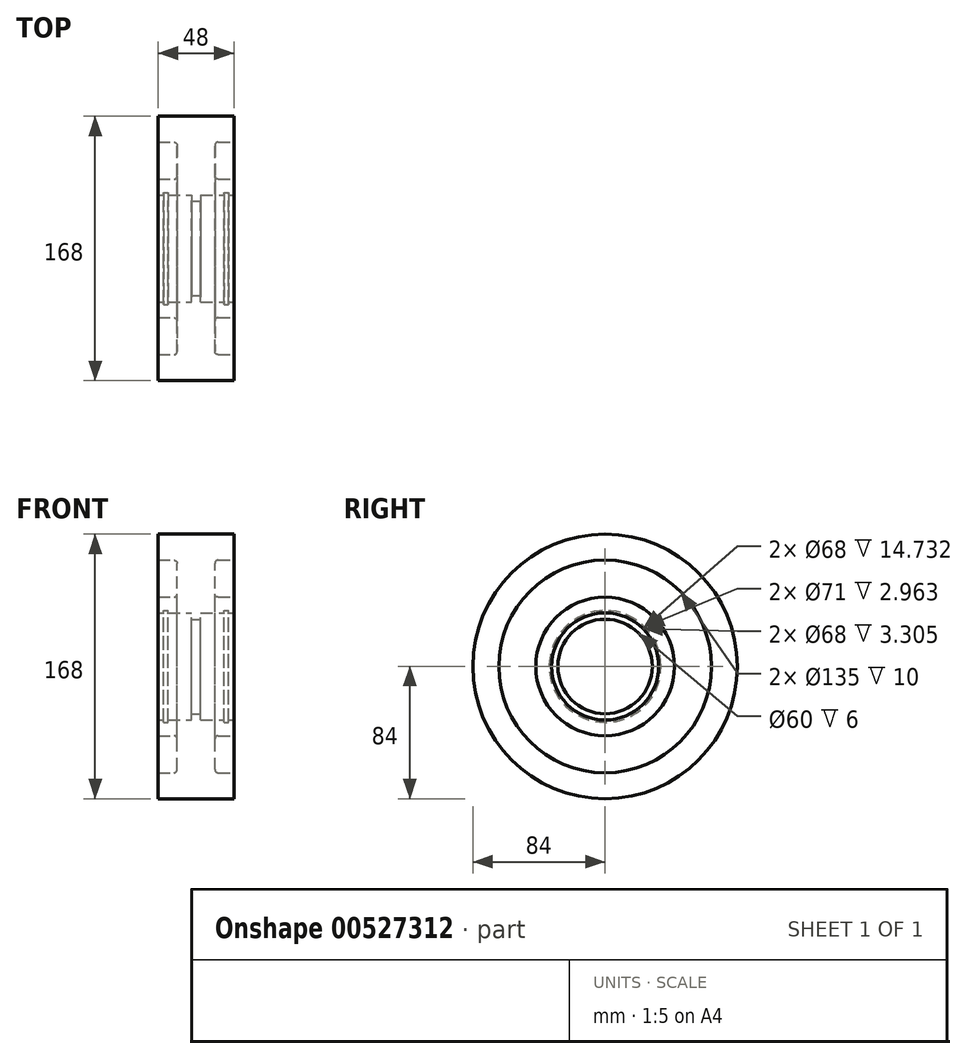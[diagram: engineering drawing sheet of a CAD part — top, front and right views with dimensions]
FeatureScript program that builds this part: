
annotation { "Feature Type Name" : "Feature", "Feature Type Description" : "" }
export const myFeature = defineFeature(function(context is Context, id is Id, definition is map)
    precondition{}
    {
        {
            var Q0;
            Q0=qCreatedBy(makeId("Front.planeOp"),FACE);
            var sketch = newSketch(context, id + "F0", { "sketchPlane" : qUnion([Q0])});
            skLineSegment(sketch, "E0.bottom", {"start": v(0, 0) * mm, "end": v(-24, 0) * mm});
            skLineSegment(sketch, "E0.top", {"start": v(0, 84) * mm, "end": v(-24, 84) * mm});
            skLineSegment(sketch, "E0.left", {"start": v(0, 0) * mm, "end": v(0, 84) * mm});
            skLineSegment(sketch, "E0.right", {"start": v(-24, 34) * mm, "end": v(-24, 44) * mm});
            skLineSegment(sketch, "E1", {"start": v(-24, 34) * mm, "end": v(-20.7, 34) * mm});
            skLineSegment(sketch, "E2", {"start": v(-20.7, 34) * mm, "end": v(-20.7, 35.5) * mm});
            skLineSegment(sketch, "E3", {"start": v(-20.7, 35.5) * mm, "end": v(-17.73, 35.5) * mm});
            skLineSegment(sketch, "E4", {"start": v(-17.73, 35.5) * mm, "end": v(-17.73, 34) * mm});
            skLineSegment(sketch, "E5", {"start": v(-17.73, 34) * mm, "end": v(-3, 34) * mm});
            skLineSegment(sketch, "E6", {"start": v(-3, 34) * mm, "end": v(-3, 30) * mm});
            skLineSegment(sketch, "E7", {"start": v(-3, 30) * mm, "end": v(0, 30) * mm});
            skLineSegment(sketch, "E8", {"start": v(-24, 44) * mm, "end": v(-14, 44) * mm});
            skLineSegment(sketch, "E9", {"start": v(-12, 46) * mm, "end": v(-12, 65.5) * mm});
            skLineSegment(sketch, "E10", {"start": v(-14, 67.5) * mm, "end": v(-24, 67.5) * mm});
            skPoint(sketch, "E11.visualSharp", {"position": v(-12, 67.5) * mm});
            skArc(sketch, "E11.filletArc", {"start": v(-12, 65.5) * mm, "mid": v(-12.59, 66.91) * mm, "end": v(-14, 67.5) * mm});
            skPoint(sketch, "E12.visualSharp", {"position": v(-12, 44) * mm});
            skArc(sketch, "E12.filletArc", {"start": v(-14, 44) * mm, "mid": v(-12.59, 44.59) * mm, "end": v(-12, 46) * mm});
            skLineSegment(sketch, "E13.trimOffspring", {"start": v(-24, 67.5) * mm, "end": v(-24, 84) * mm});
            skLineSegment(sketch, "E14.MirrorCS", {"start": v(0, 84) * mm, "end": v(24, 84) * mm});
            skLineSegment(sketch, "E15.MirrorCS", {"start": v(24, 67.5) * mm, "end": v(24, 84) * mm});
            skLineSegment(sketch, "E16.MirrorCS", {"start": v(14, 67.5) * mm, "end": v(24, 67.5) * mm});
            skArc(sketch, "E17.MirrorCS", {"start": v(12, 65.5) * mm, "mid": v(12.59, 66.91) * mm, "end": v(14, 67.5) * mm});
            skLineSegment(sketch, "E18.MirrorCS", {"start": v(12, 46) * mm, "end": v(12, 65.5) * mm});
            skArc(sketch, "E19.MirrorCS", {"start": v(14, 44) * mm, "mid": v(12.59, 44.59) * mm, "end": v(12, 46) * mm});
            skLineSegment(sketch, "E20.MirrorCS", {"start": v(24, 44) * mm, "end": v(14, 44) * mm});
            skLineSegment(sketch, "E21.MirrorCS", {"start": v(24, 34) * mm, "end": v(24, 44) * mm});
            skLineSegment(sketch, "E22.MirrorCS", {"start": v(24, 34) * mm, "end": v(20.7, 34) * mm});
            skLineSegment(sketch, "E23.MirrorCS", {"start": v(20.7, 35.5) * mm, "end": v(17.73, 35.5) * mm});
            skLineSegment(sketch, "E24.MirrorCS", {"start": v(20.7, 34) * mm, "end": v(20.7, 35.5) * mm});
            skLineSegment(sketch, "E25.MirrorCS", {"start": v(17.73, 35.5) * mm, "end": v(17.73, 34) * mm});
            skLineSegment(sketch, "E26.MirrorCS", {"start": v(17.73, 34) * mm, "end": v(3, 34) * mm});
            skLineSegment(sketch, "E27.MirrorCS", {"start": v(3, 34) * mm, "end": v(3, 30) * mm});
            skLineSegment(sketch, "E28.MirrorCS", {"start": v(3, 30) * mm, "end": v(0, 30) * mm});
            skSolve(sketch);
        }
        {
            var Q0;
            {var subQ1=sQuery(id+"F0.wireOp",EDGE,"E0.top");Q0=makeQuery(id+"F0.imprint","IMPRINT",FACE,{"disambiguationData":[TD([[makeQuery(id+"F0.imprint","IMPRINT",EDGE,{"derivedFrom":subQ1}),1.0]])]});}
            var Q1;
            {var subQ0=sQuery(id+"F0.wireOp",EDGE,"E14.MirrorCS");Q1=makeQuery(id+"F0.imprint","IMPRINT",FACE,{"disambiguationData":[TD([[makeQuery(id+"F0.imprint","IMPRINT",EDGE,{"derivedFrom":subQ0}),-1.0]])]});}
            var Q2;
            Q2=sQuery(id+"F0.wireOp",EDGE,"E0.bottom");
            revolve(context, id + "F1", {"entities" : qUnion([Q0, Q1]), "axis" : qUnion([Q2]), "revolveType" : RevolveType.FULL});
        }
    });
